FCSTD DOCUMENT  (FreeCAD 0.21R33668 +26 (Git))
Label: BoxAssembly
License: All rights reserved
LicenseURL: http://en.wikipedia.org/wiki/All_rights_reserved
objects: App::Link×2
EXTERNAL_REF file=BoxBody.FCStd obj=Body
EXTERNAL_REF file=BoxLid.FCStd obj=Body

FEATURE [App::Link] Link  label="Cuerpo"
  LinkedObject = -> <external BoxBody.FCStd>#Body
FEATURE [App::Link] Link001  label="Cuerpo001"
  LinkPlacement = pos=(1.22609e-05,1.66595e-05,140.249) rot=(0,1,0;3.14159rad)
  LinkedObject = -> <external BoxLid.FCStd>#Body
  Placement = pos=(1.22609e-05,1.66595e-05,140.249) rot=(0,1,0;3.14159rad)

RESOLVED EXTERNAL PARTS (link-assembly join: the EXTERNAL_REF files above that resolve inside this repo's crawl, each included once):
---- part BoxBody.FCStd = doc fcstd_35452efe5c76 ----
FCSTD DOCUMENT  (FreeCAD 0.21R33668 +26 (Git))
Label: BoxBody
License: All rights reserved
LicenseURL: http://en.wikipedia.org/wiki/All_rights_reserved
objects: Sketcher::SketchObject×9, PartDesign::Pad×7, PartDesign::Thickness×1, PartDesign::Hole×1, PartDesign::Mirrored×1, PartDesign::Pocket×1, PartDesign::Body×1
note: 31 computed .brp shape members not serialized (recipe doc carries the construction recipe); baked Part::Feature solids carry a one-line shape summary decoded from their .brp

FEATURE [Sketcher::SketchObject] Sketch
  FullyConstrained = true
  MapMode = 5
  Support = -> [XY_Plane]
  sketch-geometry (4):
    g0: LineSegment StartX=-52.5 StartY=52.5 StartZ=0 EndX=52.5 EndY=52.5 EndZ=0
    g1: LineSegment StartX=52.5 StartY=52.5 StartZ=0 EndX=52.5 EndY=-52.5 EndZ=0
    g2: LineSegment StartX=52.5 StartY=-52.5 StartZ=0 EndX=-52.5 EndY=-52.5 EndZ=0
    g3: LineSegment StartX=-52.5 StartY=-52.5 StartZ=0 EndX=-52.5 EndY=52.5 EndZ=0
  constraints (11):
    c: Coincident(g0,g1)
    c: Coincident(g1,g2)
    c: Coincident(g2,g3)
    c: Coincident(g3,g0)
    c: Horizontal(g0)
    c: Horizontal(g2)
    c: Vertical(g1)
    c: Vertical(g3)
    c: Symmetric(g0,g1,g-1)
    c: DistanceY(g2,g0) = 105
    c: DistanceX(g0,g0) = 105
FEATURE [PartDesign::Pad] Pad
  Direction = (0,0,1)
  Length = 105
  Length2 = 10
  Profile = -> Sketch
  ReferenceAxis = -> Sketch [N_Axis]
  Type = 0
FEATURE [PartDesign::Thickness] Thickness
  Base = -> Pad [Face6]
  BaseFeature = -> Pad
  Intersection = false
  Join = 0
  Mode = 0
  Reversed = true
  SupportTransform = false
  Value = 5
FEATURE [Sketcher::SketchObject] Sketch001
  FullyConstrained = false
  MapMode = 5
  Placement = pos=(0,0,0) rot=(1,0,0;3.14159rad)
  Support = -> [Thickness]
  sketch-geometry (4):
    g0: Circle CenterX=-40 CenterY=40 CenterZ=0 NormalX=0 NormalY=0 NormalZ=1 AngleXU=0 Radius=4
    g1: Circle CenterX=40 CenterY=40 CenterZ=0 NormalX=0 NormalY=0 NormalZ=1 AngleXU=0 Radius=4
    g2: Circle CenterX=-40 CenterY=-40 CenterZ=0 NormalX=0 NormalY=0 NormalZ=1 AngleXU=0 Radius=4
    g3: Circle CenterX=40 CenterY=-40 CenterZ=0 NormalX=0 NormalY=0 NormalZ=1 AngleXU=0 Radius=4
  constraints (5):
    c: Diameter(g0) = 8
    c: Equal(g1,g3)
    c: Equal(g3,g2)
    c: Equal(g2,g0)
    c: DistanceY(g3,g1) = 80
FEATURE [PartDesign::Pad] Pad001
  BaseFeature = -> Thickness
  Direction = (0,0,-1)
  Length = 100
  Length2 = 10
  Profile = -> Sketch001
  ReferenceAxis = -> Sketch001 [N_Axis]
  Reversed = true
  Type = 0
  expr: Length = Pad.Length - Thickness.Value
FEATURE [Sketcher::SketchObject] Sketch002
  ExternalGeometry = -> [Pad001]
  FullyConstrained = true
  MapMode = 5
  Placement = pos=(0,0,100) rot=(0,0,1;0rad)
  Support = -> [Pad001]
  sketch-geometry (2):
    g0: Circle CenterX=-40 CenterY=40 CenterZ=0 NormalX=0 NormalY=0 NormalZ=1 AngleXU=0 Radius=4
    g1: Circle CenterX=-40 CenterY=-40 CenterZ=0 NormalX=0 NormalY=0 NormalZ=1 AngleXU=0 Radius=4
  constraints (4):
    c: Coincident(g0,g-3)
    c: Coincident(g1,g-4)
    c: Equal(g1,g-4)
    c: Equal(g0,g-3)
FEATURE [PartDesign::Hole] Hole
  BaseFeature = -> Pad001
  CustomThreadClearance = 0
  Depth = 15
  DepthType = 0
  Diameter = 3.4
  DrillForDepth = false
  DrillPoint = 1
  DrillPointAngle = 118
  HoleCutCountersinkAngle = 90
  HoleCutCustomValues = false
  HoleCutDepth = 0
  HoleCutDiameter = 6.1
  HoleCutType = 0
  ModelThread = false
  Profile = -> Sketch002
  Tapered = false
  TaperedAngle = 90
  ThreadClass = 0
  ThreadDepth = 15
  ThreadDepthType = 0
  ThreadDirection = 0
  ThreadFit = 0
  ThreadSize = 9
  ThreadType = 1
  Threaded = false
  UseCustomThreadClearance = false
FEATURE [PartDesign::Mirrored] Mirrored
  BaseFeature = -> Hole
  MirrorPlane = -> Sketch002 [V_Axis]
  Originals = -> [Hole]
FEATURE [Sketcher::SketchObject] Sketch003
  ExternalGeometry = -> [Mirrored]
  FullyConstrained = false
  MapMode = 5
  Placement = pos=(0,0,5) rot=(0,0,1;0rad)
  Support = -> [Mirrored]
  sketch-geometry (4):
    g0: Circle CenterX=-0.117346 CenterY=7.21e-14 CenterZ=0 NormalX=0 NormalY=0 NormalZ=1 AngleXU=0 Radius=2.75
    g1: GeomPoint X=2.63262 Y=-0.0126504 Z=0
    g2: Circle CenterX=-0.133688 CenterY=0 CenterZ=0 NormalX=0 NormalY=0 NormalZ=1 AngleXU=0 Radius=4.76631
    g3: GeomPoint X=4.63262 Y=0 Z=0
  constraints (5):
    c: PointOnObject(g1,g0)
    c: PointOnObject(g3,g2)
    c: DistanceX(g1,g3) = 2
    c: DistanceY(g-4,g-1) = 47.5
    c: Diameter(g0) = 5.5
FEATURE [PartDesign::Pad] Pad002
  BaseFeature = -> Mirrored
  Direction = (0,0,1)
  Length = 11
  Length2 = 10
  Profile = -> Sketch003
  ReferenceAxis = -> Sketch003 [N_Axis]
  Type = 0
FEATURE [Sketcher::SketchObject] Sketch004
  ExternalGeometry = -> [Pad002]
  FullyConstrained = false
  MapMode = 5
  Placement = pos=(-47.5,0,0) rot=(0.57735,0.57735,0.57735;2.0944rad)
  Support = -> [Pad002]
  sketch-geometry (5):
    g0: GeomPoint X=0 Y=52.5 Z=0
    g1: Circle CenterX=0.15 CenterY=52.5 CenterZ=0 NormalX=0 NormalY=0 NormalZ=1 AngleXU=0 Radius=2.75
    g2: Circle CenterX=0 CenterY=52.5 CenterZ=0 NormalX=0 NormalY=0 NormalZ=1 AngleXU=0 Radius=4.9
    g3: GeomPoint X=2.9 Y=52.5 Z=0
    g4: GeomPoint X=4.9 Y=52.5 Z=0
  constraints (7):
    c: PointOnObject(g0,g-2)
    c: DistanceY(g-3,g0) = 47.5
    c: PointOnObject(g3,g1)
    c: PointOnObject(g4,g2)
    c: Horizontal(g4,g3)
    c: DistanceX(g3,g4) = 2
    c: Diameter(g1) = 5.5
FEATURE [PartDesign::Pad] Pad003
  BaseFeature = -> Pad002
  Direction = (1,0,0)
  Length = 11
  Length2 = 10
  Profile = -> Sketch004
  ReferenceAxis = -> Sketch004 [N_Axis]
  Type = 0
FEATURE [Sketcher::SketchObject] Sketch005
  ExternalGeometry = -> [Pad003]
  FullyConstrained = false
  MapMode = 5
  Placement = pos=(47.5,0,0) rot=(0.57735,-0.57735,-0.57735;2.0944rad)
  Support = -> [Pad003]
  sketch-geometry (5):
    g0: GeomPoint X=0 Y=52.5 Z=0
    g1: Circle CenterX=0 CenterY=52.5 CenterZ=0 NormalX=0 NormalY=0 NormalZ=1 AngleXU=0 Radius=2.75
    g2: Circle CenterX=0 CenterY=52.5 CenterZ=0 NormalX=0 NormalY=0 NormalZ=1 AngleXU=0 Radius=4.75339
    g3: GeomPoint X=2.74952 Y=52.4486 Z=0
    g4: GeomPoint X=4.74952 Y=52.3081 Z=0
  constraints (8):
    c: PointOnObject(g0,g-2)
    c: DistanceY(g-3,g0) = 47.5
    c: Coincident(g1,g0)
    c: Coincident(g2,g1)
    c: Diameter(g1) = 5.5
    c: PointOnObject(g3,g1)
    c: PointOnObject(g4,g2)
    c: DistanceX(g3,g4) = 2
FEATURE [PartDesign::Pad] Pad004
  BaseFeature = -> Pad003
  Direction = (-1,0,0)
  Length = 11
  Length2 = 10
  Profile = -> Sketch005
  ReferenceAxis = -> Sketch005 [N_Axis]
  Type = 0
FEATURE [Sketcher::SketchObject] Sketch006
  ExternalGeometry = -> [Pad004]
  FullyConstrained = true
  MapMode = 5
  Placement = pos=(0,-47.5,0) rot=(0,0.707107,0.707107;3.14159rad)
  Support = -> [Pad004]
  sketch-geometry (5):
    g0: GeomPoint X=0 Y=52.5 Z=0
    g1: Circle CenterX=0 CenterY=52.5 CenterZ=0 NormalX=0 NormalY=0 NormalZ=1 AngleXU=0 Radius=2.75
    g2: Circle CenterX=0 CenterY=52.5 CenterZ=0 NormalX=0 NormalY=0 NormalZ=1 AngleXU=0 Radius=4.75
    g3: GeomPoint X=4.75 Y=52.5 Z=0
    g4: GeomPoint X=2.75 Y=52.5 Z=0
  constraints (10):
    c: PointOnObject(g0,g-2)
    c: DistanceY(g-3,g0) = 47.5
    c: Coincident(g1,g0)
    c: Coincident(g2,g1)
    c: Diameter(g1) = 5.5
    c: PointOnObject(g3,g2)
    c: PointOnObject(g4,g1)
    c: Horizontal(g4,g3)
    c: Horizontal(g3,g1)
    c: DistanceX(g4,g3) = 2
FEATURE [PartDesign::Pad] Pad005
  BaseFeature = -> Pad004
  Direction = (0,1,-2e-16)
  Length = 11
  Length2 = 10
  Profile = -> Sketch006
  ReferenceAxis = -> Sketch006 [N_Axis]
  Type = 0
FEATURE [Sketcher::SketchObject] Sketch007
  ExternalGeometry = -> [Pad005]
  FullyConstrained = true
  MapMode = 5
  Placement = pos=(0,47.5,0) rot=(1,0,0;1.5708rad)
  Support = -> [Pad005]
  sketch-geometry (5):
    g0: GeomPoint X=0 Y=52.5 Z=0
    g1: Circle CenterX=0 CenterY=52.5 CenterZ=0 NormalX=0 NormalY=0 NormalZ=1 AngleXU=0 Radius=2.75
    g2: Circle CenterX=0 CenterY=52.5 CenterZ=0 NormalX=0 NormalY=0 NormalZ=1 AngleXU=0 Radius=4.75
    g3: GeomPoint X=2.75 Y=52.5 Z=0
    g4: GeomPoint X=4.75 Y=52.5 Z=0
  constraints (10):
    c: PointOnObject(g0,g-2)
    c: DistanceY(g-3,g0) = 47.5
    c: Coincident(g1,g0)
    c: Coincident(g2,g1)
    c: Diameter(g1) = 5.5
    c: PointOnObject(g3,g1)
    c: PointOnObject(g4,g2)
    c: Horizontal(g4,g3)
    c: Horizontal(g1,g3)
    c: DistanceX(g3,g4) = 2
FEATURE [PartDesign::Pad] Pad006
  BaseFeature = -> Pad005
  Direction = (0,-1,2e-16)
  Length = 11
  Length2 = 10
  Profile = -> Sketch007
  ReferenceAxis = -> Sketch007 [N_Axis]
  Type = 0
FEATURE [Sketcher::SketchObject] Sketch008
  FullyConstrained = false
  MapMode = 5
  Placement = pos=(0,-52.5,0) rot=(1,0,0;1.5708rad)
  Support = -> [Pad006]
  sketch-geometry (4):
    g0: LineSegment StartX=13.9411 StartY=95.2052 StartZ=0 EndX=26.9411 EndY=95.2052 EndZ=0
    g1: LineSegment StartX=26.9411 StartY=95.2052 StartZ=0 EndX=26.9411 EndY=85.2052 EndZ=0
    g2: LineSegment StartX=26.9411 StartY=85.2052 StartZ=0 EndX=13.9411 EndY=85.2052 EndZ=0
    g3: LineSegment StartX=13.9411 StartY=85.2052 StartZ=0 EndX=13.9411 EndY=95.2052 EndZ=0
  constraints (10):
    c: Coincident(g0,g1)
    c: Coincident(g1,g2)
    c: Coincident(g2,g3)
    c: Coincident(g3,g0)
    c: Horizontal(g0)
    c: Horizontal(g2)
    c: Vertical(g1)
    c: Vertical(g3)
    c: DistanceX(g0,g0) = 13
    c: DistanceY(g1,g1) = 10
FEATURE [PartDesign::Pocket] Pocket
  BaseFeature = -> Pad006
  Direction = (0,1,-2e-16)
  Length = 5
  Length2 = 5
  Profile = -> Sketch008
  ReferenceAxis = -> Sketch008 [N_Axis]
  Type = 0
FEATURE [PartDesign::Body] Body  label="Cuerpo"
  Group = -> [Sketch,Pad,Thickness,Sketch001,Pad001,Sketch002,Hole,Mirrored,Sketch003,Pad002,Sketch004,Pad003,Sketch005,Pad004,Sketch006,Pad005,Sketch007,Pad006,Sketch008,Pocket]
  Origin = -> Origin
  Tip = -> Pocket
---- part BoxLid.FCStd = doc fcstd_89234d41ae3a ----
FCSTD DOCUMENT  (FreeCAD 0.21R33668 +26 (Git))
Label: BoxLid
License: All rights reserved
LicenseURL: http://en.wikipedia.org/wiki/All_rights_reserved
objects: Sketcher::SketchObject×9, PartDesign::Pad×5, PartDesign::Pocket×2, PartDesign::SubShapeBinder×1, PartDesign::Mirrored×1, PartDesign::Hole×1, PartDesign::Body×1
note: 28 computed .brp shape members not serialized (recipe doc carries the construction recipe); baked Part::Feature solids carry a one-line shape summary decoded from their .brp
EXTERNAL_REF file=BoxBody.FCStd obj=Body

FEATURE [PartDesign::SubShapeBinder] Binder
  BindCopyOnChange = 0
  BindMode = 0
  ClaimChildren = false
  Context = -> Body [Binder.]
  Fuse = false
  MakeFace = true
  OffsetFill = false
  OffsetIntersection = false
  OffsetJoinType = 0
  OffsetOpenResult = false
  PartialLoad = false
  Relative = true
  Support = -> [<external BoxBody.FCStd>#Body[Pad001.Face5,Pad001.Face23,Pad001.Face21,Pad001.Face20,Pad001.Face22]]
  _Version = 2
FEATURE [Sketcher::SketchObject] Sketch
  ExternalGeometry = -> [Binder]
  FullyConstrained = false
  MapMode = 5
  Support = -> [XY_Plane]
  sketch-geometry (8):
    g0: LineSegment StartX=-52.5 StartY=52.5 StartZ=0 EndX=52.5 EndY=52.5 EndZ=0
    g1: LineSegment StartX=52.5 StartY=52.5 StartZ=0 EndX=52.5 EndY=-52.5 EndZ=0
    g2: LineSegment StartX=52.5 StartY=-52.5 StartZ=0 EndX=-52.5 EndY=-52.5 EndZ=0
    g3: LineSegment StartX=-52.5 StartY=-52.5 StartZ=0 EndX=-52.5 EndY=52.5 EndZ=0
    g4: GeomPoint X=-40 Y=40 Z=0
    g5: GeomPoint X=-40 Y=-40 Z=0
    g6: GeomPoint X=40 Y=-40 Z=0
    g7: GeomPoint X=40 Y=40 Z=0
  constraints (10):
    c: Coincident(g0,g1)
    c: Coincident(g1,g2)
    c: Coincident(g2,g3)
    c: Coincident(g3,g0)
    c: Horizontal(g0)
    c: Horizontal(g2)
    c: Vertical(g1)
    c: Vertical(g3)
    c: Coincident(g1,g-6)
    c: Coincident(g-3,g0)
FEATURE [PartDesign::Pad] Pad
  Direction = (0,0,1)
  Length = 5
  Length2 = 10
  Profile = -> Sketch
  ReferenceAxis = -> Sketch [N_Axis]
  Type = 0
FEATURE [Sketcher::SketchObject] Sketch001
  ExternalGeometry = -> [Binder]
  FullyConstrained = false
  MapMode = 5
  Placement = pos=(0,0,5) rot=(0,0,1;0rad)
  Support = -> [Pad]
  sketch-geometry (22):
    g0: LineSegment StartX=-30 StartY=47 StartZ=0 EndX=-5 EndY=47 EndZ=0
    g1: LineSegment StartX=-5 StartY=47 StartZ=0 EndX=-5 EndY=45.5 EndZ=0
    g2: LineSegment StartX=-5 StartY=45.5 StartZ=0 EndX=-30 EndY=45.5 EndZ=0
    g3: LineSegment StartX=-30 StartY=45.5 StartZ=0 EndX=-30 EndY=47 EndZ=0
    g4: LineSegment StartX=-30 StartY=-45.5 StartZ=0 EndX=-5 EndY=-45.5 EndZ=0
    g5: LineSegment StartX=-5 StartY=-45.5 StartZ=0 EndX=-5 EndY=-47 EndZ=0
    g6: LineSegment StartX=-5 StartY=-47 StartZ=0 EndX=-30 EndY=-47 EndZ=0
    g7: LineSegment StartX=-30 StartY=-47 StartZ=0 EndX=-30 EndY=-45.5 EndZ=0
    g8: LineSegment StartX=-47 StartY=12.5 StartZ=0 EndX=-45.5 EndY=12.5 EndZ=0
    g9: LineSegment StartX=-45.5 StartY=12.5 StartZ=0 EndX=-45.5 EndY=-12.5 EndZ=0
    g10: LineSegment StartX=-45.5 StartY=-12.5 StartZ=0 EndX=-47 EndY=-12.5 EndZ=0
    g11: LineSegment StartX=-47 StartY=-12.5 StartZ=0 EndX=-47 EndY=12.5 EndZ=0
    g12: GeomPoint X=-36 Y=40 Z=0
    g13: Circle CenterX=-40 CenterY=40 CenterZ=0 NormalX=0 NormalY=0 NormalZ=1 AngleXU=0 Radius=4.5
    g14: GeomPoint X=-35.5 Y=40 Z=0
    g15: Circle CenterX=-40 CenterY=40 CenterZ=0 NormalX=0 NormalY=0 NormalZ=1 AngleXU=0 Radius=6
    g16: GeomPoint X=-34 Y=40 Z=0
    g17: GeomPoint X=-40.1435 Y=43.9974 Z=0
    g18: GeomPoint X=-40 Y=47.5 Z=0
    g19: GeomPoint X=-47.5 Y=40 Z=0
    g20: Circle CenterX=-40 CenterY=-40 CenterZ=0 NormalX=0 NormalY=0 NormalZ=1 AngleXU=0 Radius=4.5
    g21: Circle CenterX=-40 CenterY=-40 CenterZ=0 NormalX=0 NormalY=0 NormalZ=1 AngleXU=0 Radius=6
  constraints (55):
    c: Coincident(g0,g1)
    c: Coincident(g1,g2)
    c: Coincident(g2,g3)
    c: Coincident(g3,g0)
    c: Horizontal(g0)
    c: Horizontal(g2)
    c: Vertical(g1)
    c: Vertical(g3)
    c: Coincident(g4,g5)
    c: Coincident(g5,g6)
    c: Coincident(g6,g7)
    c: Coincident(g7,g4)
    c: Horizontal(g4)
    c: Horizontal(g6)
    c: Vertical(g5)
    c: Vertical(g7)
    c: DistanceY(g-5,g6) = 0.5
    c: DistanceY(g7,g7) = 1.5
    c: DistanceX(g4,g4) = 25
    c: DistanceX(g-4,g4) = 10
    c: Vertical(g4,g2)
    c: Vertical(g1,g4)
    c: Equal(g1,g5)
    c: DistanceY(g0,g-6) = 0.5
    c: Coincident(g8,g9)
    c: Coincident(g9,g10)
    c: Coincident(g10,g11)
    c: Coincident(g11,g8)
    c: Horizontal(g8)
    c: Horizontal(g10)
    c: Vertical(g11)
    c: Equal(g8,g1)
    c: Symmetric(g8,g9,g-1)
    c: DistanceX(g-7,g8) = 0.5
    c: DistanceY(g9,g9) = 25
    c: PointOnObject(g12,g-3)
    c: Horizontal(g12,g-3)
    c: Coincident(g13,g-3)
    c: PointOnObject(g14,g13)
    c: Horizontal(g13,g14)
    c: DistanceX(g12,g14) = 0.5
    c: Coincident(g15,g13)
    c: PointOnObject(g16,g15)
    c: Horizontal(g13,g16)
    c: DistanceX(g14,g16) = 1.5
    c: PointOnObject(g18,g-6)
    c: PointOnObject(g19,g-7)
    c: Horizontal(g13,g19)
    c: Vertical(g13,g18)
    c: DistanceY(g13,g18) = 7.5
    c: DistanceX(g19,g13) = 7.5
    c: Coincident(g20,g-4)
    c: Coincident(g21,g20)
    c: Equal(g20,g13)
    c: Equal(g21,g15)
FEATURE [PartDesign::Pad] Pad001
  BaseFeature = -> Pad
  Direction = (0,0,1)
  Length = 8
  Length2 = 10
  Profile = -> Sketch001
  ReferenceAxis = -> Sketch001 [N_Axis]
  Type = 0
FEATURE [Sketcher::SketchObject] Sketch002
  ExternalGeometry = -> [Binder]
  FullyConstrained = true
  MapMode = 5
  Placement = pos=(0,0,0) rot=(1,0,0;3.14159rad)
  Support = -> [Pad001]
  sketch-geometry (2):
    g0: Circle CenterX=-40 CenterY=40 CenterZ=0 NormalX=0 NormalY=0 NormalZ=1 AngleXU=0 Radius=1.5
    g1: Circle CenterX=-40 CenterY=-40 CenterZ=0 NormalX=0 NormalY=0 NormalZ=1 AngleXU=0 Radius=1.5
  constraints (4):
    c: Coincident(g0,g-4)
    c: Coincident(g1,g-5)
    c: Diameter(g0) = 3
    c: Equal(g0,g1)
FEATURE [PartDesign::Pocket] Pocket
  BaseFeature = -> Pad001
  Direction = (0,0,1)
  Length = 5
  Length2 = 5
  Profile = -> Sketch002
  ReferenceAxis = -> Sketch002 [N_Axis]
  Type = 1
FEATURE [Sketcher::SketchObject] Sketch003
  ExternalGeometry = -> [Pocket]
  FullyConstrained = true
  MapMode = 5
  Placement = pos=(0,0,0) rot=(1,0,0;3.14159rad)
  Support = -> [Pocket]
  sketch-geometry (2):
    g0: Circle CenterX=-40 CenterY=40 CenterZ=0 NormalX=0 NormalY=0 NormalZ=1 AngleXU=0 Radius=2
    g1: Circle CenterX=-40 CenterY=-40 CenterZ=0 NormalX=0 NormalY=0 NormalZ=1 AngleXU=0 Radius=2
  constraints (4):
    c: Coincident(g0,g-3)
    c: Coincident(g1,g-4)
    c: Equal(g0,g1)
    c: Diameter(g0) = 4
FEATURE [PartDesign::Pocket] Pocket001
  BaseFeature = -> Pocket
  Direction = (0,0,1)
  Length = 2.5
  Length2 = 5
  Profile = -> Sketch003
  ReferenceAxis = -> Sketch003 [N_Axis]
  Type = 0
FEATURE [PartDesign::Mirrored] Mirrored
  BaseFeature = -> Pocket001
  MirrorPlane = -> Sketch001 [V_Axis]
  Originals = -> [Pad001,Pocket,Pocket001]
FEATURE [Sketcher::SketchObject] Sketch004
  FullyConstrained = true
  MapMode = 5
  Placement = pos=(0,0,5) rot=(0,0,1;0rad)
  Support = -> [Mirrored]
  sketch-geometry (4):
    g0: Circle CenterX=0 CenterY=0 CenterZ=0 NormalX=0 NormalY=0 NormalZ=1 AngleXU=0 Radius=2.75
    g1: Circle CenterX=0 CenterY=0 CenterZ=0 NormalX=0 NormalY=0 NormalZ=1 AngleXU=0 Radius=4.75
    g2: GeomPoint X=2.75 Y=0 Z=0
    g3: GeomPoint X=4.75 Y=0 Z=0
  constraints (8):
    c: Coincident(g0,g-1)
    c: Coincident(g1,g0)
    c: Diameter(g0) = 5.5
    c: PointOnObject(g2,g0)
    c: PointOnObject(g3,g1)
    c: Horizontal(g2,g3)
    c: Horizontal(g3,g0)
    c: DistanceX(g2,g3) = 2
FEATURE [PartDesign::Pad] Pad002
  BaseFeature = -> Mirrored
  Direction = (0,0,1)
  Length = 10
  Length2 = 10
  Profile = -> Sketch004
  ReferenceAxis = -> Sketch004 [N_Axis]
  Type = 0
FEATURE [Sketcher::SketchObject] Sketch005  label="S2MiniSize"
  ExternalGeometry = -> [Binder]
  FullyConstrained = false
  MapMode = 5
  Placement = pos=(0,0,5) rot=(0,0,1;0rad)
  Support = -> [Pad002]
  sketch-geometry (12):
    g0: ArcOfCircle CenterX=-29.1788 CenterY=35.8299 CenterZ=0 NormalX=0 NormalY=0 NormalZ=1 AngleXU=0 Radius=2.5 StartAngle=1.5708 EndAngle=3.14159
    g1: LineSegment StartX=-29.1788 StartY=38.3299 StartZ=0 EndX=-8.77882 EndY=38.3299 EndZ=0
    g2: ArcOfCircle CenterX=-8.77882 CenterY=35.8299 CenterZ=0 NormalX=0 NormalY=0 NormalZ=1 AngleXU=0 Radius=2.5 StartAngle=0 EndAngle=1.5708
    g3: LineSegment StartX=-6.27882 StartY=35.8299 StartZ=0 EndX=-6.27882 EndY=6.52989 EndZ=0
    g4: ArcOfCircle CenterX=-8.77882 CenterY=6.52989 CenterZ=0 NormalX=0 NormalY=0 NormalZ=1 AngleXU=0 Radius=2.5 StartAngle=4.71239 EndAngle=6.28319
    g5: LineSegment StartX=-8.77882 StartY=4.02989 StartZ=0 EndX=-29.1788 EndY=4.02989 EndZ=0
    g6: ArcOfCircle CenterX=-29.1788 CenterY=6.52989 CenterZ=0 NormalX=0 NormalY=0 NormalZ=1 AngleXU=0 Radius=2.5 StartAngle=3.14159 EndAngle=4.71239
    g7: LineSegment StartX=-31.6788 StartY=6.52989 StartZ=0 EndX=-31.6788 EndY=35.8299 EndZ=0
    g8: GeomPoint X=-31.6788 Y=38.3299 Z=0
    g9: GeomPoint X=-6.27882 Y=4.02989 Z=0
    g10: Circle CenterX=-29.1788 CenterY=35.8299 CenterZ=0 NormalX=0 NormalY=0 NormalZ=1 AngleXU=0 Radius=1
    g11: Circle CenterX=-8.77882 CenterY=35.8299 CenterZ=0 NormalX=0 NormalY=0 NormalZ=1 AngleXU=0 Radius=1
  constraints (27):
    c: Tangent(g0,g1) = 1.5708
    c: Tangent(g1,g2) = 1.5708
    c: Tangent(g2,g3) = 1.5708
    c: Tangent(g3,g4) = 1.5708
    c: Tangent(g4,g5) = 1.5708
    c: Tangent(g5,g6) = 1.5708
    c: Tangent(g6,g7) = 1.5708
    c: Tangent(g7,g0) = 1.5708
    c: Horizontal(g1)
    c: Horizontal(g5)
    c: Vertical(g3)
    c: Vertical(g7)
    c: Equal(g0,g2)
    c: Equal(g2,g4)
    c: Equal(g4,g6)
    c: PointOnObject(g8,g1)
    c: PointOnObject(g8,g7)
    c: PointOnObject(g9,g3)
    c: PointOnObject(g9,g5)
    c: DistanceY(g4,g1) = 34.3
    c: DistanceX(g0,g2) = 25.4
    c: DistanceX(g0,g0) = 2.5
    c: DistanceX(g0,g2) = 20.4
    c: Coincident(g10,g0)
    c: Coincident(g11,g2)
    c: Equal(g11,g10)
    c: Diameter(g11) = 2
FEATURE [Sketcher::SketchObject] Sketch006
  ExternalGeometry = -> [Sketch005]
  FullyConstrained = true
  MapMode = 5
  Placement = pos=(0,0,5) rot=(0,0,1;0rad)
  Support = -> [Pad002]
  sketch-geometry (4):
    g0: Circle CenterX=-29.1788 CenterY=35.8299 CenterZ=0 NormalX=0 NormalY=0 NormalZ=1 AngleXU=0 Radius=2.5
    g1: Circle CenterX=-8.77882 CenterY=35.8299 CenterZ=0 NormalX=0 NormalY=0 NormalZ=1 AngleXU=0 Radius=2.5
    g2: GeomPoint X=-26.6788 Y=35.8299 Z=0
    g3: GeomPoint X=-28.1788 Y=35.8299 Z=0
  constraints (8):
    c: Coincident(g0,g-3)
    c: Coincident(g1,g-4)
    c: PointOnObject(g2,g0)
    c: PointOnObject(g3,g-3)
    c: Horizontal(g0,g2)
    c: Horizontal(g3,g0)
    c: DistanceX(g3,g2) = 1.5
    c: Equal(g0,g1)
FEATURE [PartDesign::Pad] Pad003
  BaseFeature = -> Pad002
  Direction = (0,0,1)
  Length = 10
  Length2 = 10
  Profile = -> Sketch006
  ReferenceAxis = -> Sketch006 [N_Axis]
  Type = 0
FEATURE [Sketcher::SketchObject] Sketch007
  ExternalGeometry = -> [Pad003]
  FullyConstrained = false
  MapMode = 5
  Placement = pos=(0,0,15) rot=(0,0,1;0rad)
  Support = -> [Pad003]
  sketch-geometry (2):
    g0: Circle CenterX=-29.1788 CenterY=35.8299 CenterZ=0 NormalX=0 NormalY=0 NormalZ=1 AngleXU=0 Radius=2.5
    g1: Circle CenterX=-8.77882 CenterY=35.8299 CenterZ=0 NormalX=0 NormalY=0 NormalZ=1 AngleXU=0 Radius=2.5
  constraints (3):
    c: Coincident(g0,g-3)
    c: Coincident(g1,g-4)
    c: Equal(g0,g1)
FEATURE [PartDesign::Hole] Hole
  BaseFeature = -> Pad003
  CustomThreadClearance = 0
  Depth = 5
  DepthType = 0
  Diameter = 2.52
  DrillForDepth = false
  DrillPoint = 1
  DrillPointAngle = 118
  HoleCutCountersinkAngle = 90
  HoleCutCustomValues = false
  HoleCutDepth = 0
  HoleCutDiameter = 6.1
  HoleCutType = 0
  ModelThread = true
  Profile = -> Sketch007
  Tapered = false
  TaperedAngle = 90
  ThreadClass = 0
  ThreadDepth = 5
  ThreadDepthType = 0
  ThreadDirection = 0
  ThreadFit = 0
  ThreadSize = 9
  ThreadType = 1
  Threaded = true
  UseCustomThreadClearance = false
FEATURE [Sketcher::SketchObject] Sketch008
  FullyConstrained = false
  MapMode = 5
  Placement = pos=(0,0,5) rot=(0,0,1;0rad)
  Support = -> [Hole]
  sketch-geometry (4):
    g0: LineSegment StartX=-22.7788 StartY=11.3299 StartZ=0 EndX=-14.7788 EndY=11.3299 EndZ=0
    g1: LineSegment StartX=-14.7788 StartY=11.3299 StartZ=0 EndX=-14.7788 EndY=4.32989 EndZ=0
    g2: LineSegment StartX=-14.7788 StartY=4.32989 StartZ=0 EndX=-22.7788 EndY=4.32989 EndZ=0
    g3: LineSegment StartX=-22.7788 StartY=4.32989 StartZ=0 EndX=-22.7788 EndY=11.3299 EndZ=0
  constraints (10):
    c: Coincident(g0,g1)
    c: Coincident(g1,g2)
    c: Coincident(g2,g3)
    c: Coincident(g3,g0)
    c: Horizontal(g0)
    c: Horizontal(g2)
    c: Vertical(g1)
    c: Vertical(g3)
    c: DistanceY(g1,g1) = 7
    c: DistanceX(g2,g1) = 8
FEATURE [PartDesign::Pad] Pad004
  BaseFeature = -> Hole
  Direction = (0,0,1)
  Length = 7
  Length2 = 10
  Profile = -> Sketch008
  ReferenceAxis = -> Sketch008 [N_Axis]
  Type = 0
FEATURE [PartDesign::Body] Body  label="Cuerpo"
  Group = -> [Binder,Sketch,Pad,Sketch001,Pad001,Sketch002,Pocket,Sketch003,Pocket001,Mirrored,Sketch004,Pad002,Sketch005,Sketch006,Pad003,Sketch007,Hole,Sketch008,Pad004]
  Origin = -> Origin
  Tip = -> Pad004
